# Revit family: Kitchen_Taps-Mixers_hansgrohe_72827XXX-Talis-M54-Single-lever-kitchen_
name_source: partatom
category: Plumbing Fixtures
revit_build: Autodesk Revit 2015 (Build: 20140903_1530(x64)
units: mm (PartAtom-declared; Revit-internal decimal feet)

## types (3) — shared parameters
BIMobject category = Taps & Mixers
BIMobject category code = kitchen-taps
BIMobject main category = Kitchen
BIMobject main category code = kitchen
Brand url = http://www.hansgrohe-int.com
Default Elevation = 1219.2 mm  [stored 4 ft]
Design country = Germany
Edition number = 1
GTIN code = https://4059625277928
IFC Classification = Sanitary Terminal
Installation instructions = https://www.hansgrohe.com
Manufacturer country = Germany
Manufacturer name = hansgrohe
Material main = Chrome
Product Guid = 61ad3b05-519f-4877-a9ac-13d00ff1c254
Product SKU = 72827XXX
Product data url = https://bimobject.com
Product family = Talis M54
Product group = Kitchen mixers
Product name = 72827XXX Talis M54 Single lever kitchen mixer 270, device shut-off valve, 1jet
Product url = https://www.hansgrohe.com
QR code = http://bimobject.com
Technical description = https://www.hansgrohe.com

## type names (no varying parameters)
- 000 Chrome
- 670 Matte Black
- 800 Stainless Steel Finish

note: [stored X ft] marks values corroborated as IEEE doubles in the binary element streams (Revit-internal decimal feet)

## geometry (parser evidence)
native form markers: Sweep x4
no freeform markers — native parametric forms only
